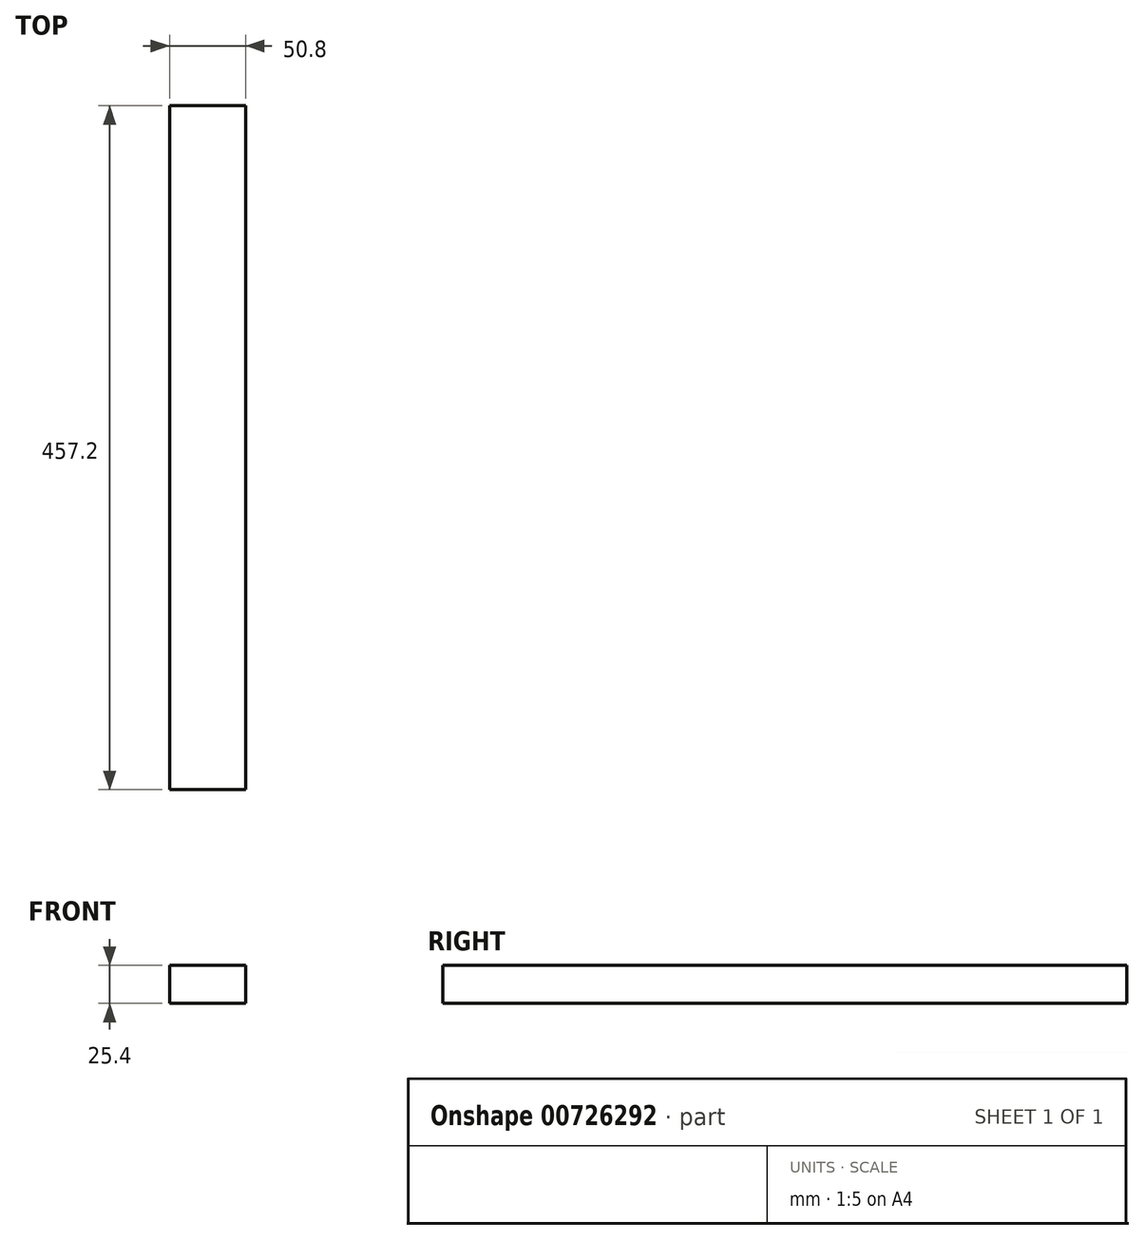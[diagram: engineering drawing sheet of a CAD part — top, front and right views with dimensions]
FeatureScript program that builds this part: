
annotation { "Feature Type Name" : "Feature", "Feature Type Description" : "" }
export const myFeature = defineFeature(function(context is Context, id is Id, definition is map)
    precondition{}
    {
        {
            var Q0;
            Q0=qCreatedBy(makeId("Front.planeOp"),FACE);
            var sketch = newSketch(context, id + "F0", { "sketchPlane" : qUnion([Q0])});
            skLineSegment(sketch, "E0.bottom", {"start": v(-26.04, 9.57) * mm, "end": v(24.76, 9.57) * mm});
            skLineSegment(sketch, "E0.top", {"start": v(-26.04, -15.83) * mm, "end": v(24.76, -15.83) * mm});
            skLineSegment(sketch, "E0.left", {"start": v(-26.04, 9.57) * mm, "end": v(-26.04, -15.83) * mm});
            skLineSegment(sketch, "E0.right", {"start": v(24.76, 9.57) * mm, "end": v(24.76, -15.83) * mm});
            skSolve(sketch);
        }
        {
            var Q0;
            Q0 = qSketchRegion(id + "F0", true);
            extrude(context, id + "F1", {"entities" : qUnion([Q0]), "endBound" : BoundingType.SYMMETRIC, "depth" : 457.2 * mm, "offsetDistance" : 25.4 * mm});
        }
    });
